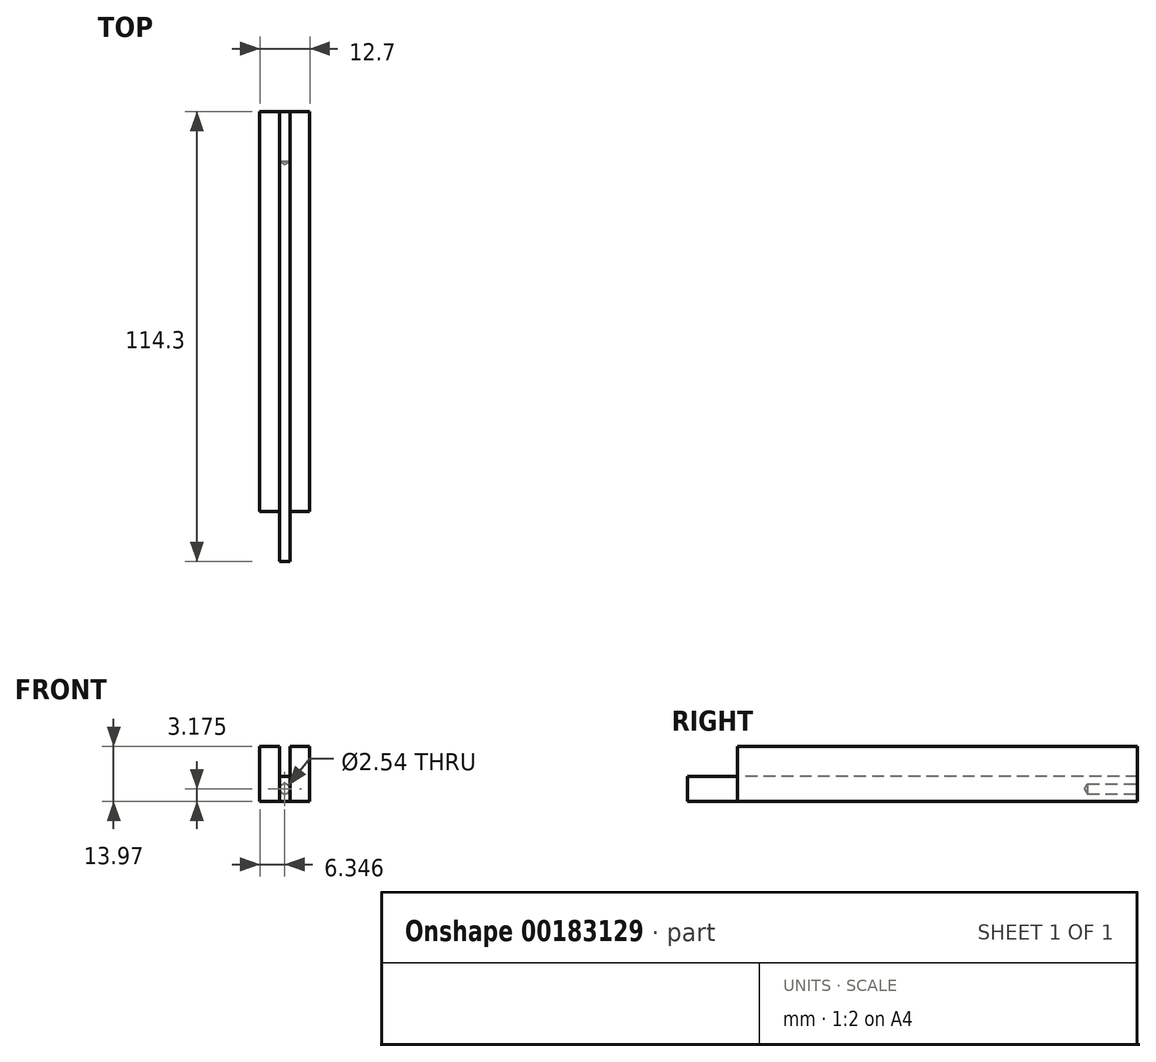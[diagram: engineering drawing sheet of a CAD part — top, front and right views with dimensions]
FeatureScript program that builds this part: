
annotation { "Feature Type Name" : "Feature", "Feature Type Description" : "" }
export const myFeature = defineFeature(function(context is Context, id is Id, definition is map)
    precondition{}
    {
        {
            var Q0;
            Q0=qCreatedBy(makeId("Top.planeOp"),FACE);
            var sketch = newSketch(context, id + "F0", { "sketchPlane" : qUnion([Q0])});
            skLineSegment(sketch, "E0.bottom", {"start": v(-7.06, 89.34) * mm, "end": v(5.64, 89.34) * mm});
            skLineSegment(sketch, "E0.top", {"start": v(-7.06, -12.26) * mm, "end": v(5.64, -12.26) * mm});
            skLineSegment(sketch, "E0.left", {"start": v(-7.06, 89.34) * mm, "end": v(-7.06, -12.26) * mm});
            skLineSegment(sketch, "E0.right", {"start": v(5.64, 89.34) * mm, "end": v(5.64, -12.26) * mm});
            skSolve(sketch);
        }
        {
            var Q0;
            Q0 = qSketchRegion(id + "F0", true);
            extrude(context, id + "F1", {"entities" : qUnion([Q0]), "depth" : 6.35 * mm});
        }
        {
            var Q0;
            Q0=makeQuery(id+"F1.opExtrude","CAP_FACE",FACE,{"disambiguationData":[OSD([sQuery(id+"F0.wireOp",EDGE,"E0.bottom"),sQuery(id+"F0.wireOp",EDGE,"E0.top"),sQuery(id+"F0.wireOp",EDGE,"E0.left"),sQuery(id+"F0.wireOp",EDGE,"E0.right")])],"isStart":false});
            var sketch = newSketch(context, id + "F2", { "sketchPlane" : qUnion([Q0])});
            skLineSegment(sketch, "E1.left", {"start": v(-7.06, 89.34) * mm, "end": v(-7.06, -12.26) * mm});
            skLineSegment(sketch, "E1.right", {"start": v(5.64, 89.34) * mm, "end": v(5.64, -12.26) * mm});
            skLineSegment(sketch, "E2.0", {"start": v(0.56, 89.34) * mm, "end": v(0.56, -12.26) * mm});
            skLineSegment(sketch, "E3.0", {"start": v(-1.98, 89.34) * mm, "end": v(-1.98, -12.26) * mm});
            skLineSegment(sketch, "E4", {"start": v(-7.06, 89.34) * mm, "end": v(-1.98, 89.34) * mm});
            skLineSegment(sketch, "E5", {"start": v(0.56, 89.34) * mm, "end": v(5.64, 89.34) * mm});
            skLineSegment(sketch, "E6", {"start": v(0.56, -12.26) * mm, "end": v(5.64, -12.26) * mm});
            skLineSegment(sketch, "E7", {"start": v(-1.98, -12.26) * mm, "end": v(-7.06, -12.26) * mm});
            skSolve(sketch);
        }
        {
            var Q0;
            Q0 = qSketchRegion(id + "F2", true);
            extrude(context, id + "F3", {"entities" : qUnion([Q0]), "operationType" : NewBodyOperationType.ADD, "depth" : 7.62 * mm});
        }
        {
            var Q0;
            Q0=makeQuery(id+"F3.boolean.opBoolean","MERGE",FACE,{"derivedFrom":[makeQuery(id+"F1.opExtrude","SWEPT_FACE",FACE,{"disambiguationData":[OSD([sQuery(id+"F0.wireOp",EDGE,"E0.top")])]}),makeQuery(id+"F3.opExtrude","SWEPT_FACE",FACE,{"disambiguationData":[OSD([sQuery(id+"F2.wireOp",EDGE,"E6")])]}),makeQuery(id+"F3.opExtrude","SWEPT_FACE",FACE,{"disambiguationData":[OSD([sQuery(id+"F2.wireOp",EDGE,"E7")])]})]});
            var sketch = newSketch(context, id + "F4", { "sketchPlane" : qUnion([Q0])});
            skLineSegment(sketch, "E8.bottom", {"start": v(-1.98, 6.35) * mm, "end": v(0.56, 6.35) * mm});
            skLineSegment(sketch, "E8.top", {"start": v(-1.98, 0) * mm, "end": v(0.56, 0) * mm});
            skLineSegment(sketch, "E8.left", {"start": v(-1.98, 6.35) * mm, "end": v(-1.98, 0) * mm});
            skLineSegment(sketch, "E8.right", {"start": v(0.56, 6.35) * mm, "end": v(0.56, 0) * mm});
            skSolve(sketch);
        }
        {
            var Q0;
            Q0 = qSketchRegion(id + "F4", true);
            extrude(context, id + "F5", {"entities" : qUnion([Q0]), "operationType" : NewBodyOperationType.ADD, "depth" : 12.7 * mm});
        }
        {
            var Q0;
            Q0=makeQuery(id+"F3.boolean.opBoolean","MERGE",FACE,{"derivedFrom":[makeQuery(id+"F1.opExtrude","SWEPT_FACE",FACE,{"disambiguationData":[OSD([sQuery(id+"F0.wireOp",EDGE,"E0.bottom")])]}),makeQuery(id+"F3.opExtrude","SWEPT_FACE",FACE,{"disambiguationData":[OSD([sQuery(id+"F2.wireOp",EDGE,"E4")])]}),makeQuery(id+"F3.opExtrude","SWEPT_FACE",FACE,{"disambiguationData":[OSD([sQuery(id+"F2.wireOp",EDGE,"E5")])]})]});
            var sketch = newSketch(context, id + "F6", { "sketchPlane" : qUnion([Q0])});
            skPoint(sketch, "E9.startSnap0", {"position": v(-5.64, 6.99) * mm});
            skPoint(sketch, "E10", {"position": v(0.71, 3.18) * mm});
            skLineSegment(sketch, "E11.bottom", {"start": v(-5.64, 13.97) * mm, "end": v(7.06, 13.97) * mm});
            skLineSegment(sketch, "E11.top", {"start": v(-5.64, 0) * mm, "end": v(7.06, 0) * mm});
            skLineSegment(sketch, "E11.left", {"start": v(-5.64, 13.97) * mm, "end": v(-5.64, 0) * mm});
            skLineSegment(sketch, "E11.right", {"start": v(7.06, 13.97) * mm, "end": v(7.06, 0) * mm});
            skSolve(sketch);
        }
        {
            var Q0;
            Q0=sQuery(id+"F6.wireOp",VERTEX,"E10");
            var Q1;
            Q1=makeQuery(id+"F1.opExtrude","SWEPT_BODY",BODY,{"disambiguationData":[OSD([sQuery(id+"F0.wireOp",EDGE,"E0.bottom"),sQuery(id+"F0.wireOp",EDGE,"E0.top"),sQuery(id+"F0.wireOp",EDGE,"E0.left"),sQuery(id+"F0.wireOp",EDGE,"E0.right")])]});
            hole(context, id + "F7", {"style" : HoleStyle.SIMPLE, "endStyle" : HoleEndStyle.BLIND, "holeDiameter" : 2.54 * mm, "holeDepth" : 12.7 * mm, "locations" : qUnion([Q0]), "scope" : qUnion([Q1])});
        }
    });
